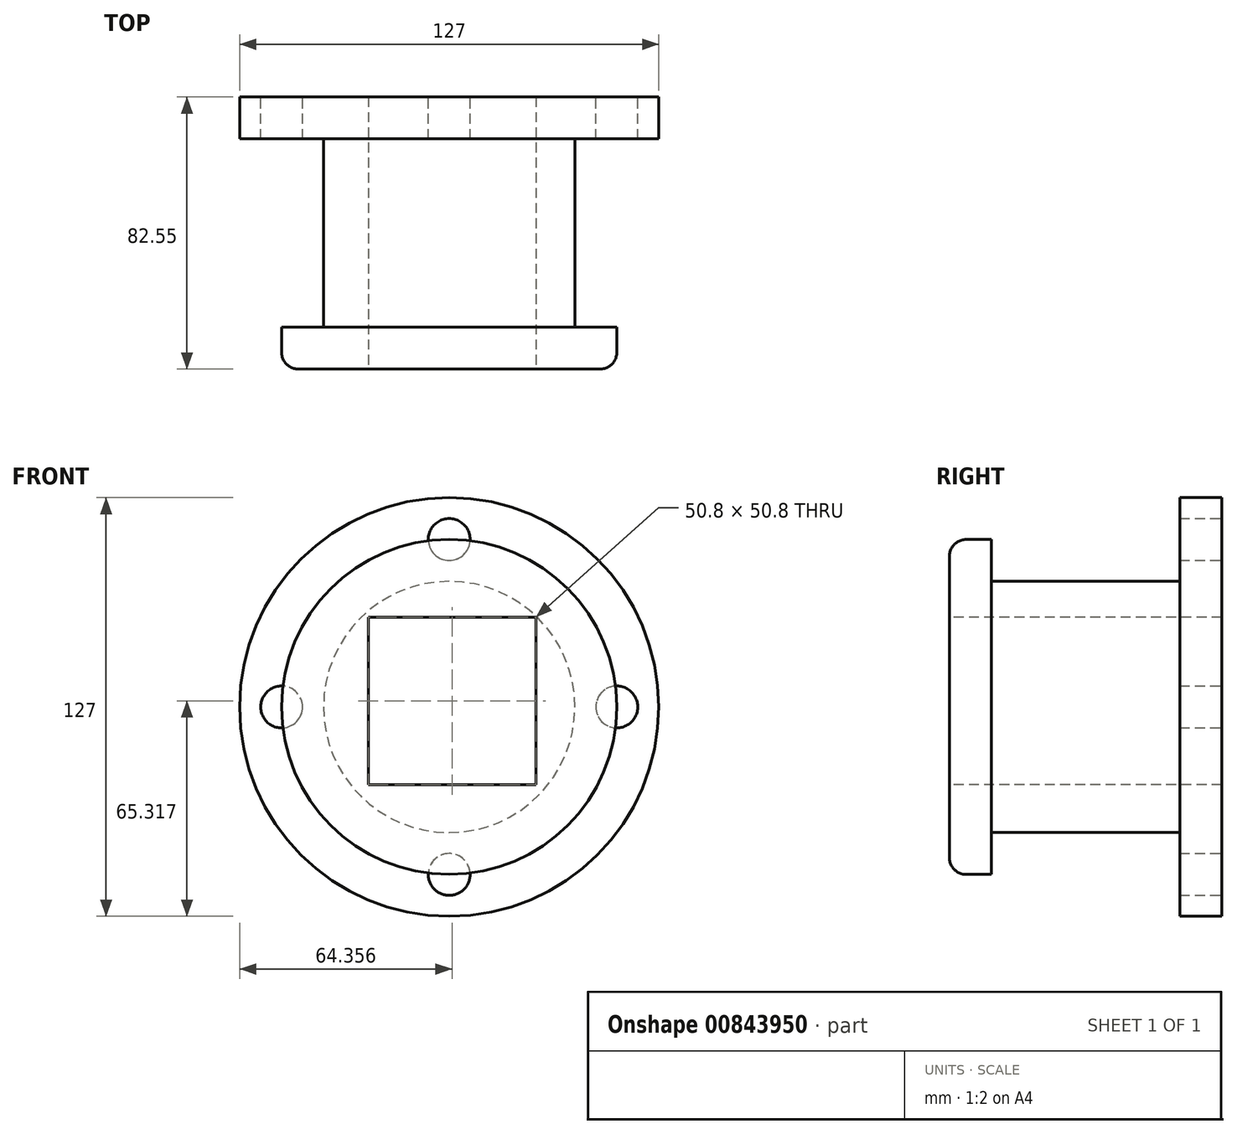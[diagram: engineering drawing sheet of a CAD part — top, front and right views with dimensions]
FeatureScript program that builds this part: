
annotation { "Feature Type Name" : "Feature", "Feature Type Description" : "" }
export const myFeature = defineFeature(function(context is Context, id is Id, definition is map)
    precondition{}
    {
        {
            var Q0;
            Q0=qCreatedBy(makeId("Front.planeOp"),FACE);
            var sketch = newSketch(context, id + "F0", { "sketchPlane" : qUnion([Q0])});
            skCircle(sketch, "E0", {"center": v(0, 0) * mm, "radius": 63.5 * mm});
            skLineSegment(sketch, "E1", {"start": v(0, 0) * mm, "end": v(0, 50.8) * mm});
            skCircle(sketch, "E2", {"center": v(0, 50.8) * mm, "radius": 6.35 * mm});
            skLineSegment(sketch, "E3", {"start": v(0, 0) * mm, "end": v(-50.8, 0) * mm});
            skCircle(sketch, "E4", {"center": v(-50.8, 0) * mm, "radius": 6.35 * mm});
            skLineSegment(sketch, "E5", {"start": v(0, 0) * mm, "end": v(50.8, 0) * mm});
            skCircle(sketch, "E6", {"center": v(50.8, 0) * mm, "radius": 6.35 * mm});
            skLineSegment(sketch, "E7", {"start": v(0, 0) * mm, "end": v(0, -50.8) * mm});
            skCircle(sketch, "E8", {"center": v(0, -50.8) * mm, "radius": 6.35 * mm});
            skSolve(sketch);
        }
        {
            var Q0;
            Q0 = qSketchRegion(id + "F0", true);
            var Q1;
            Q1=makeQuery(id+"F0.imprint","IMPRINT",FACE,{"disambiguationData":[TD([[makeQuery(id+"F0.imprint","IMPRINT",EDGE,{"derivedFrom":sQuery(id+"F0.wireOp",EDGE,"E0")}),1.0]])]});
            extrude(context, id + "F1", {"entities" : qUnion([Q0, Q1]), "depth" : 12.7 * mm, "offsetDistance" : 25.4 * mm});
        }
        {
            var Q0;
            Q0=makeQuery(id+"F1.opExtrude","CAP_FACE",FACE,{"disambiguationData":[OSD([sQuery(id+"F0.wireOp",EDGE,"E0")])],"isStart":false});
            var sketch = newSketch(context, id + "F2", { "sketchPlane" : qUnion([Q0])});
            skCircle(sketch, "E9", {"center": v(0, 0) * mm, "radius": 38.1 * mm});
            skSolve(sketch);
        }
        {
            var Q0;
            Q0=makeQuery(id+"F2.imprint","IMPRINT",FACE,{"disambiguationData":[TD([[makeQuery(id+"F2.imprint","IMPRINT",EDGE,{"derivedFrom":sQuery(id+"F2.wireOp",EDGE,"E9")}),1.0]])]});
            extrude(context, id + "F3", {"entities" : qUnion([Q0]), "operationType" : NewBodyOperationType.ADD, "depth" : 57.15 * mm, "offsetDistance" : 25.4 * mm});
        }
        {
            var Q0;
            Q0=makeQuery(id+"F3.opExtrude","CAP_FACE",FACE,{"disambiguationData":[OSD([sQuery(id+"F2.wireOp",EDGE,"E9")])],"isStart":false});
            var sketch = newSketch(context, id + "F4", { "sketchPlane" : qUnion([Q0])});
            skCircle(sketch, "E10", {"center": v(0, 0) * mm, "radius": 50.8 * mm});
            skSolve(sketch);
        }
        {
            var Q0;
            Q0 = qSketchRegion(id + "F4", true);
            extrude(context, id + "F5", {"entities" : qUnion([Q0]), "operationType" : NewBodyOperationType.ADD, "depth" : 12.7 * mm, "offsetDistance" : 25.4 * mm});
        }
        {
            var Q0;
            Q0=makeQuery(id+"F5.opExtrude","CAP_FACE",FACE,{"disambiguationData":[OSD([sQuery(id+"F4.wireOp",EDGE,"E10")])],"isStart":false});
            var sketch = newSketch(context, id + "F6", { "sketchPlane" : qUnion([Q0])});
            skLineSegment(sketch, "E11.bottom", {"start": v(-24.54, 27.22) * mm, "end": v(26.26, 27.22) * mm});
            skLineSegment(sketch, "E11.top", {"start": v(-24.54, -23.58) * mm, "end": v(26.26, -23.58) * mm});
            skLineSegment(sketch, "E11.left", {"start": v(-24.54, 27.22) * mm, "end": v(-24.54, -23.58) * mm});
            skLineSegment(sketch, "E11.right", {"start": v(26.26, 27.22) * mm, "end": v(26.26, -23.58) * mm});
            skSolve(sketch);
        }
        {
            var Q0;
            Q0=makeQuery(id+"F6.imprint","IMPRINT",FACE,{"disambiguationData":[TD([[makeQuery(id+"F6.imprint","IMPRINT",EDGE,{"derivedFrom":sQuery(id+"F6.wireOp",EDGE,"E11.bottom")}),-1.0]])]});
            extrude(context, id + "F7", {"entities" : qUnion([Q0]), "operationType" : NewBodyOperationType.REMOVE, "oppositeDirection" : true, "depth" : 101.6 * mm, "offsetDistance" : 25.4 * mm});
        }
        {
            var Q0;
            Q0=makeQuery(id+"F5.opExtrude","CAP_EDGE",EDGE,{"disambiguationData":[OSD([sQuery(id+"F4.wireOp",EDGE,"E10")])],"isStart":false});
            fillet(context, id + "F8", {"entities" : qUnion([Q0]), "radius" : 5.08 * mm, "tangentPropagation" : true, "allowEdgeOverflow" : false});
        }
    });
